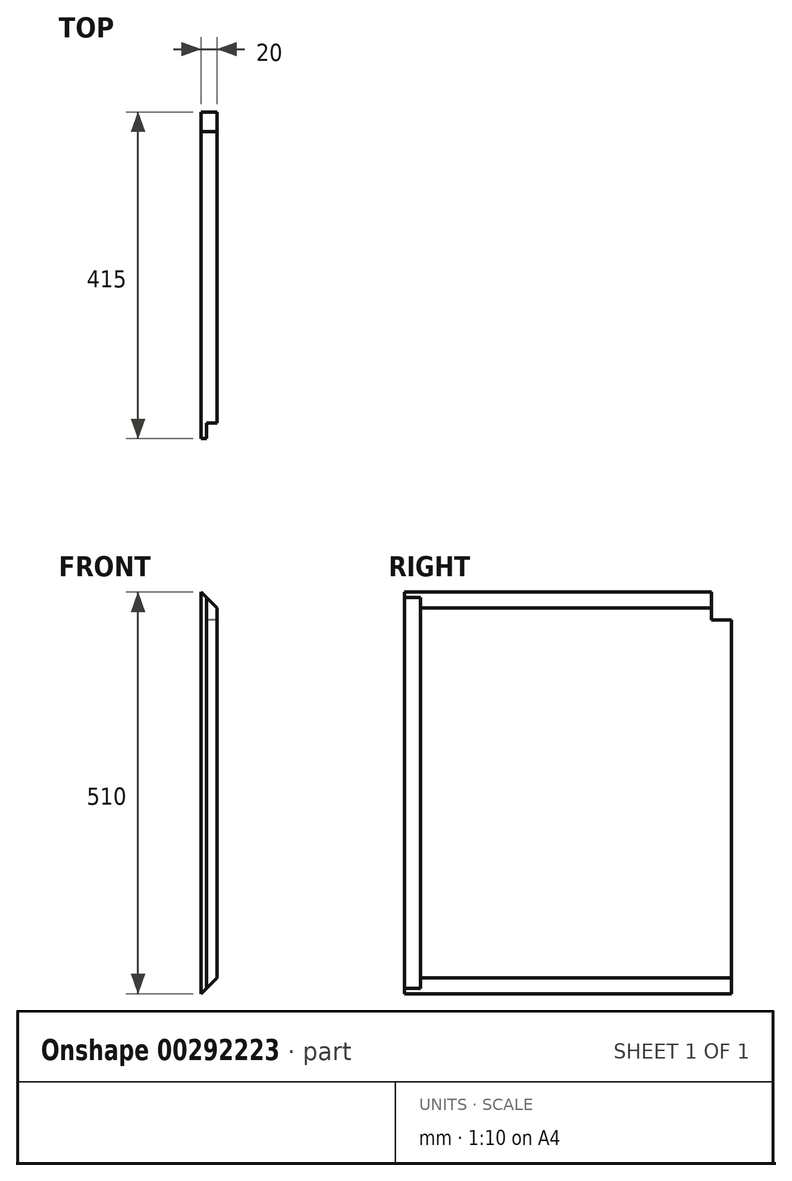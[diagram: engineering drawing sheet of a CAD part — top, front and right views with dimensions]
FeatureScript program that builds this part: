
annotation { "Feature Type Name" : "Feature", "Feature Type Description" : "" }
export const myFeature = defineFeature(function(context is Context, id is Id, definition is map)
    precondition{}
    {
        {
            var Q0;
            Q0=qCreatedBy(makeId("Right.planeOp"),FACE);
            var sketch = newSketch(context, id + "F0", { "sketchPlane" : qUnion([Q0])});
            skLineSegment(sketch, "E0.bottom", {"start": v(207.5, 255) * mm, "end": v(-207.5, 255) * mm});
            skLineSegment(sketch, "E0.top", {"start": v(207.5, -255) * mm, "end": v(-207.5, -255) * mm});
            skLineSegment(sketch, "E0.left", {"start": v(207.5, 255) * mm, "end": v(207.5, -255) * mm});
            skLineSegment(sketch, "E0.right", {"start": v(-207.5, 255) * mm, "end": v(-207.5, -255) * mm});
            skPoint(sketch, "E0.middle", {"position": v(0, 0) * mm});
            skSolve(sketch);
        }
        {
            var Q0;
            Q0=qSketchRegion(id+"F0",true);
            extrude(context, id + "F1", {"entities" : qUnion([Q0]), "depth" : 20 * mm});
        }
        {
            var Q0;
            Q0=makeQuery(id+"F1.opExtrude","SWEPT_FACE",FACE,{"disambiguationData":[OSD([sQuery(id+"F0.wireOp",EDGE,"E0.bottom")])]});
            var sketch = newSketch(context, id + "F2", { "sketchPlane" : qUnion([Q0])});
            skLineSegment(sketch, "E1.bottom", {"start": v(20, -207.5) * mm, "end": v(7, -207.5) * mm});
            skLineSegment(sketch, "E1.top", {"start": v(20, -187.5) * mm, "end": v(7, -187.5) * mm});
            skLineSegment(sketch, "E1.left", {"start": v(20, -207.5) * mm, "end": v(20, -187.5) * mm});
            skLineSegment(sketch, "E1.right", {"start": v(7, -207.5) * mm, "end": v(7, -187.5) * mm});
            skSolve(sketch);
        }
        {
            var Q0;
            Q0=qSketchRegion(id+"F2",true);
            extrude(context, id + "F3", {"entities" : qUnion([Q0]), "operationType" : NewBodyOperationType.REMOVE, "oppositeDirection" : true, "depth" : 510 * mm});
        }
        {
            var Q0;
            Q0=makeQuery(id+"F1.opExtrude","SWEPT_FACE",FACE,{"disambiguationData":[OSD([sQuery(id+"F0.wireOp",EDGE,"E0.left")])]});
            var sketch = newSketch(context, id + "F4", { "sketchPlane" : qUnion([Q0])});
            skLineSegment(sketch, "E2", {"start": v(0, 255) * mm, "end": v(-20, 235) * mm});
            skLineSegment(sketch, "E3", {"start": v(-20, 235) * mm, "end": v(-20, 255) * mm});
            skLineSegment(sketch, "E4", {"start": v(-20, 255) * mm, "end": v(0, 255) * mm});
            skLineSegment(sketch, "E5", {"start": v(0, -255) * mm, "end": v(-20, -235) * mm});
            skLineSegment(sketch, "E6", {"start": v(-20, -235) * mm, "end": v(-20, -255) * mm});
            skLineSegment(sketch, "E7", {"start": v(-20, -255) * mm, "end": v(0, -255) * mm});
            skSolve(sketch);
        }
        {
            var Q0;
            Q0=qSketchRegion(id+"F4",true);
            extrude(context, id + "F5", {"entities" : qUnion([Q0]), "operationType" : NewBodyOperationType.REMOVE, "oppositeDirection" : true, "depth" : 475 * mm});
        }
        {
            var Q0;
            Q0=makeQuery(id+"F1.opExtrude","CAP_FACE",FACE,{"disambiguationData":[OSD([sQuery(id+"F0.wireOp",EDGE,"E0.bottom"),sQuery(id+"F0.wireOp",EDGE,"E0.top"),sQuery(id+"F0.wireOp",EDGE,"E0.left"),sQuery(id+"F0.wireOp",EDGE,"E0.right")])],"isStart":true});
            var sketch = newSketch(context, id + "F6", { "sketchPlane" : qUnion([Q0])});
            skLineSegment(sketch, "E8.bottom", {"start": v(-207.5, 255) * mm, "end": v(-182.5, 255) * mm});
            skLineSegment(sketch, "E8.top", {"start": v(-207.5, 220) * mm, "end": v(-182.5, 220) * mm});
            skLineSegment(sketch, "E8.left", {"start": v(-207.5, 255) * mm, "end": v(-207.5, 220) * mm});
            skLineSegment(sketch, "E8.right", {"start": v(-182.5, 255) * mm, "end": v(-182.5, 220) * mm});
            skSolve(sketch);
        }
        {
            var Q0;
            Q0=qSketchRegion(id+"F6",true);
            extrude(context, id + "F7", {"entities" : qUnion([Q0]), "operationType" : NewBodyOperationType.REMOVE, "oppositeDirection" : true, "depth" : 25 * mm});
        }
    });
